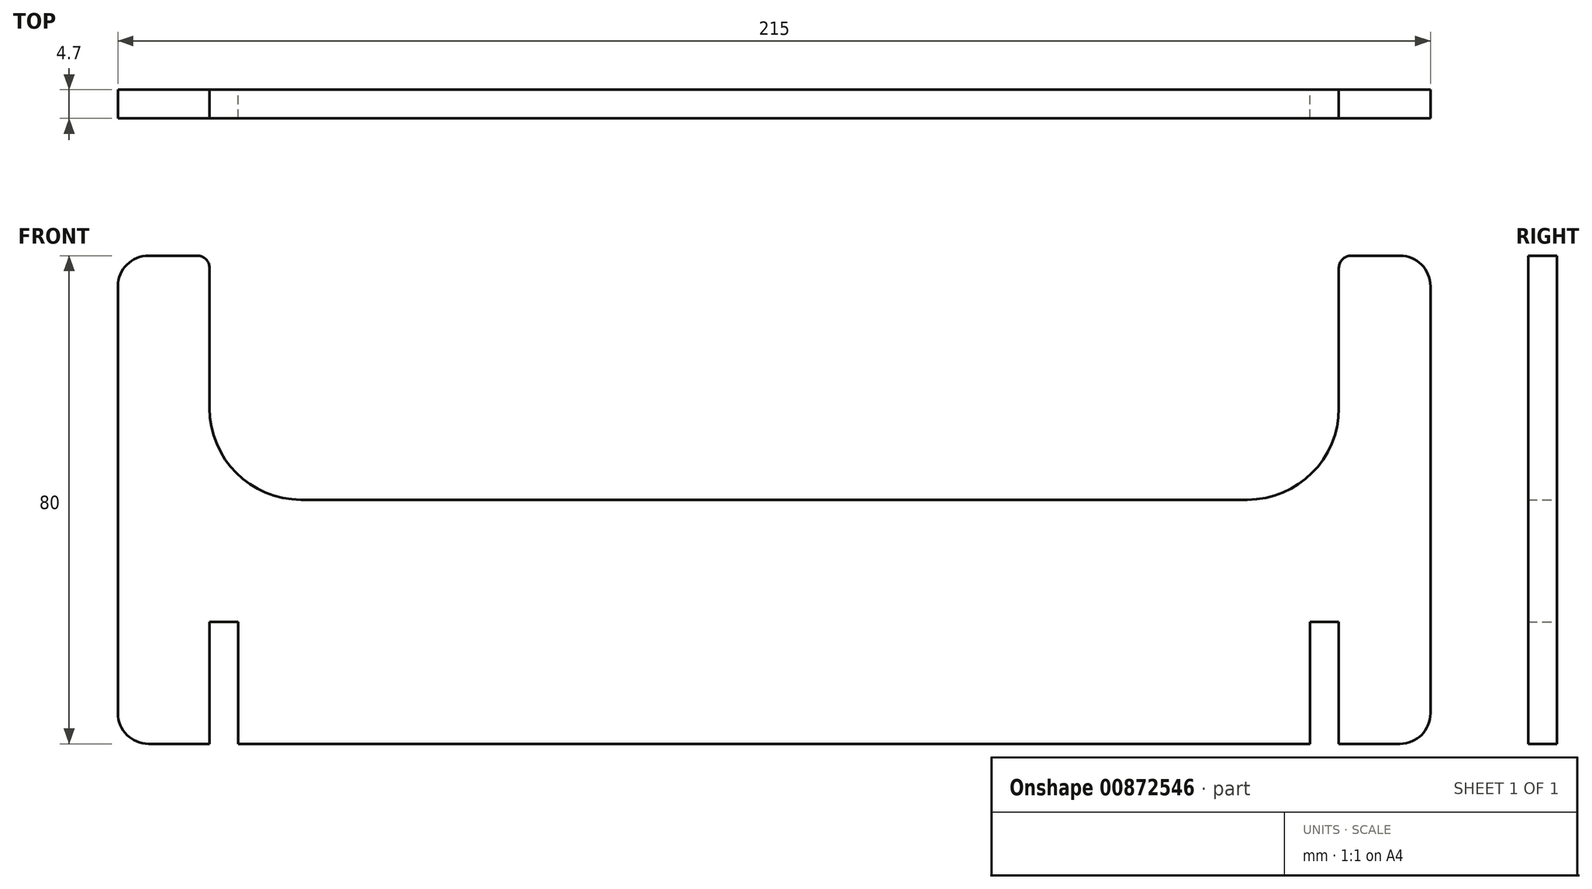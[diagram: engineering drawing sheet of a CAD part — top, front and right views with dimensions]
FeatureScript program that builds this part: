
annotation { "Feature Type Name" : "Feature", "Feature Type Description" : "" }
export const myFeature = defineFeature(function(context is Context, id is Id, definition is map)
    precondition{}
    {
        {
            assignVariable(context, id + "F0", {"name" : "e", "anyValue" : 4.7});
        }
        {
            var Q0;
            Q0=qCreatedBy(makeId("Front.planeOp"),FACE);
            var sketch = newSketch(context, id + "F1", { "sketchPlane" : qUnion([Q0])});
            skLineSegment(sketch, "E0", {"start": v(-92.5, 38) * mm, "end": v(-92.5, 15) * mm});
            skLineSegment(sketch, "E1", {"start": v(92.5, 15) * mm, "end": v(92.5, 38) * mm});
            skLineSegment(sketch, "E2", {"start": v(94.5, 40) * mm, "end": v(102.5, 40) * mm});
            skLineSegment(sketch, "E3", {"start": v(107.5, 35) * mm, "end": v(107.5, -35) * mm});
            skLineSegment(sketch, "E4", {"start": v(102.5, -40) * mm, "end": v(92.5, -40) * mm});
            skLineSegment(sketch, "E5", {"start": v(-107.5, -35) * mm, "end": v(-107.5, 35) * mm});
            skLineSegment(sketch, "E6", {"start": v(-102.5, 40) * mm, "end": v(-94.5, 40) * mm});
            skLineSegment(sketch, "E7", {"start": v(-77.5, 0) * mm, "end": v(77.5, 0) * mm});
            skPoint(sketch, "E8.visualSharp", {"position": v(-92.5, 0) * mm});
            skArc(sketch, "E8.filletArc", {"start": v(-92.5, 15) * mm, "mid": v(-88.1, 4.4) * mm, "end": v(-77.5, 0) * mm});
            skPoint(sketch, "E9.visualSharp", {"position": v(92.5, 0) * mm});
            skArc(sketch, "E9.filletArc", {"start": v(77.5, 0) * mm, "mid": v(88.1, 4.4) * mm, "end": v(92.5, 15) * mm});
            skPoint(sketch, "E10.visualSharp", {"position": v(-107.5, 40) * mm});
            skArc(sketch, "E10.filletArc", {"start": v(-102.5, 40) * mm, "mid": v(-106.04, 38.54) * mm, "end": v(-107.5, 35) * mm});
            skPoint(sketch, "E11.visualSharp", {"position": v(107.5, 40) * mm});
            skArc(sketch, "E11.filletArc", {"start": v(107.5, 35) * mm, "mid": v(106.04, 38.54) * mm, "end": v(102.5, 40) * mm});
            skPoint(sketch, "E12.visualSharp", {"position": v(-92.5, 40) * mm});
            skArc(sketch, "E12.filletArc", {"start": v(-92.5, 38) * mm, "mid": v(-93.09, 39.41) * mm, "end": v(-94.5, 40) * mm});
            skPoint(sketch, "E13.visualSharp", {"position": v(92.5, 40) * mm});
            skArc(sketch, "E13.filletArc", {"start": v(94.5, 40) * mm, "mid": v(93.09, 39.41) * mm, "end": v(92.5, 38) * mm});
            skPoint(sketch, "E14.visualSharp", {"position": v(-107.5, -40) * mm});
            skArc(sketch, "E14.filletArc", {"start": v(-107.5, -35) * mm, "mid": v(-106.04, -38.54) * mm, "end": v(-102.5, -40) * mm});
            skPoint(sketch, "E15.visualSharp", {"position": v(107.5, -40) * mm});
            skArc(sketch, "E15.filletArc", {"start": v(102.5, -40) * mm, "mid": v(106.04, -38.54) * mm, "end": v(107.5, -35) * mm});
            skLineSegment(sketch, "E16", {"start": v(-92.5, -40) * mm, "end": v(-92.5, -20) * mm});
            skLineSegment(sketch, "E17", {"start": v(-92.5, -20) * mm, "end": v(-87.8, -20) * mm});
            skLineSegment(sketch, "E18", {"start": v(-87.8, -20) * mm, "end": v(-87.8, -40) * mm});
            skLineSegment(sketch, "E19.trimOffspring", {"start": v(-92.5, -40) * mm, "end": v(-102.5, -40) * mm});
            skLineSegment(sketch, "E20", {"start": v(87.8, -40) * mm, "end": v(87.8, -20) * mm});
            skLineSegment(sketch, "E21", {"start": v(87.8, -20) * mm, "end": v(92.5, -20) * mm});
            skLineSegment(sketch, "E22", {"start": v(92.5, -20) * mm, "end": v(92.5, -40) * mm});
            skLineSegment(sketch, "E23.trimOffspring", {"start": v(87.8, -40) * mm, "end": v(-87.8, -40) * mm});
            skPoint(sketch, "E24", {"position": v(0, 0) * mm});
            skLineSegment(sketch, "E25", {"start": v(-102.5, 40) * mm, "end": v(98.5, 40) * mm, "construction": true});
            skPoint(sketch, "E26", {"position": v(98.5, 40) * mm});
            skSolve(sketch);
        }
        {
            var Q0;
            Q0=makeQuery(id+"F1.imprint","IMPRINT",FACE,{"disambiguationData":[TD([[makeQuery(id+"F1.imprint","IMPRINT",EDGE,{"derivedFrom":sQuery(id+"F1.wireOp",EDGE,"E0")}),-1.0]])]});
            extrude(context, id + "F2", {"entities" : qUnion([Q0]), "depth" : (getVariable(context, 'e')) * mm, "offsetDistance" : 25 * mm});
        }
    });
